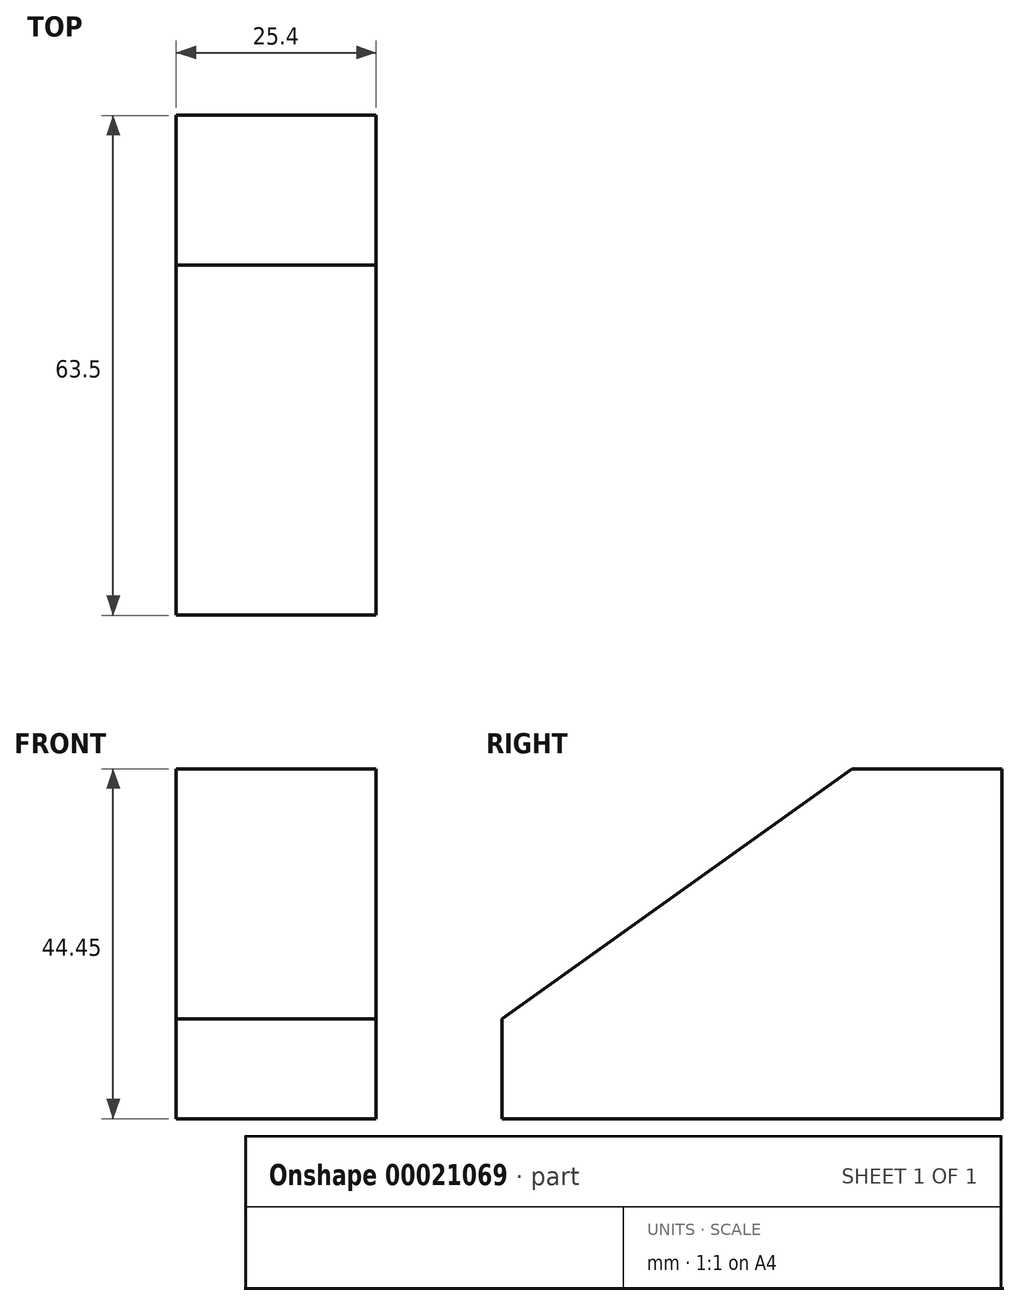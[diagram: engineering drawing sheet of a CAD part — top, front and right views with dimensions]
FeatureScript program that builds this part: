
annotation { "Feature Type Name" : "Feature", "Feature Type Description" : "" }
export const myFeature = defineFeature(function(context is Context, id is Id, definition is map)
    precondition{}
    {
        {
            var Q0;
            Q0=qCreatedBy(makeId("Right.planeOp"),FACE);
            var sketch = newSketch(context, id + "F0", { "sketchPlane" : qUnion([Q0])});
            skLineSegment(sketch, "E0", {"start": v(-16.79, 26.8) * mm, "end": v(2.26, 26.8) * mm});
            skLineSegment(sketch, "E1", {"start": v(2.26, 26.8) * mm, "end": v(2.26, -17.66) * mm});
            skLineSegment(sketch, "E2", {"start": v(-61.24, -17.66) * mm, "end": v(2.26, -17.66) * mm});
            skLineSegment(sketch, "E3", {"start": v(-61.24, -17.66) * mm, "end": v(-61.24, -4.96) * mm});
            skLineSegment(sketch, "E4", {"start": v(-61.24, -4.96) * mm, "end": v(-16.79, 26.8) * mm});
            skSolve(sketch);
        }
        {
            var Q0;
            Q0=makeQuery(id+"F0.imprint","IMPRINT",FACE,{"disambiguationData":[TD([[makeQuery(id+"F0.imprint","IMPRINT",EDGE,{"derivedFrom":sQuery(id+"F0.wireOp",EDGE,"E0")}),-1.0]])]});
            extrude(context, id + "F1", {"entities" : qUnion([Q0]), "depth" : 25.4 * mm});
        }
    });
